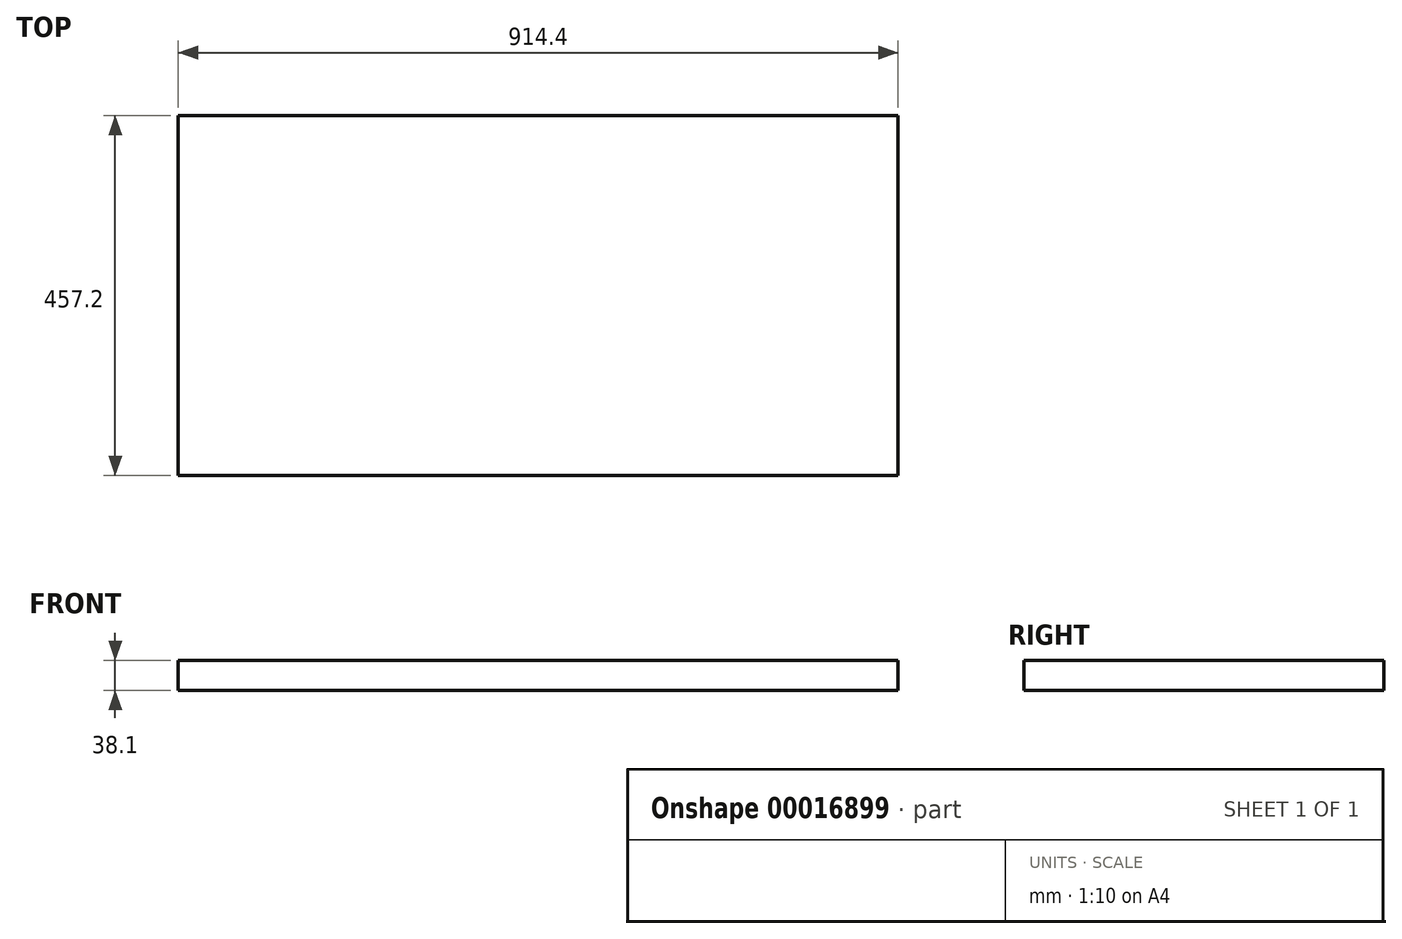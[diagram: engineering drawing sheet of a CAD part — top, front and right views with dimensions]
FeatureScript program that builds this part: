
annotation { "Feature Type Name" : "Feature", "Feature Type Description" : "" }
export const myFeature = defineFeature(function(context is Context, id is Id, definition is map)
    precondition{}
    {
        {
            var Q0;
            Q0=qCreatedBy(makeId("Top.planeOp"),FACE);
            var sketch = newSketch(context, id + "F0", { "sketchPlane" : qUnion([Q0])});
            skLineSegment(sketch, "E0.bottom", {"start": v(-457.36, 233.33) * mm, "end": v(457.04, 233.33) * mm});
            skLineSegment(sketch, "E0.top", {"start": v(-457.36, -223.87) * mm, "end": v(457.04, -223.87) * mm});
            skLineSegment(sketch, "E0.left", {"start": v(-457.36, 233.33) * mm, "end": v(-457.36, -223.87) * mm});
            skLineSegment(sketch, "E0.right", {"start": v(457.04, 233.33) * mm, "end": v(457.04, -223.87) * mm});
            skSolve(sketch);
        }
        {
            var Q0;
            Q0=makeQuery(id+"F0.imprint","IMPRINT",FACE,{"disambiguationData":[TD([[makeQuery(id+"F0.imprint","IMPRINT",EDGE,{"derivedFrom":sQuery(id+"F0.wireOp",EDGE,"E0.bottom")}),-1.0]])]});
            extrude(context, id + "F1", {"entities" : qUnion([Q0]), "depth" : 38.1 * mm});
        }
    });
